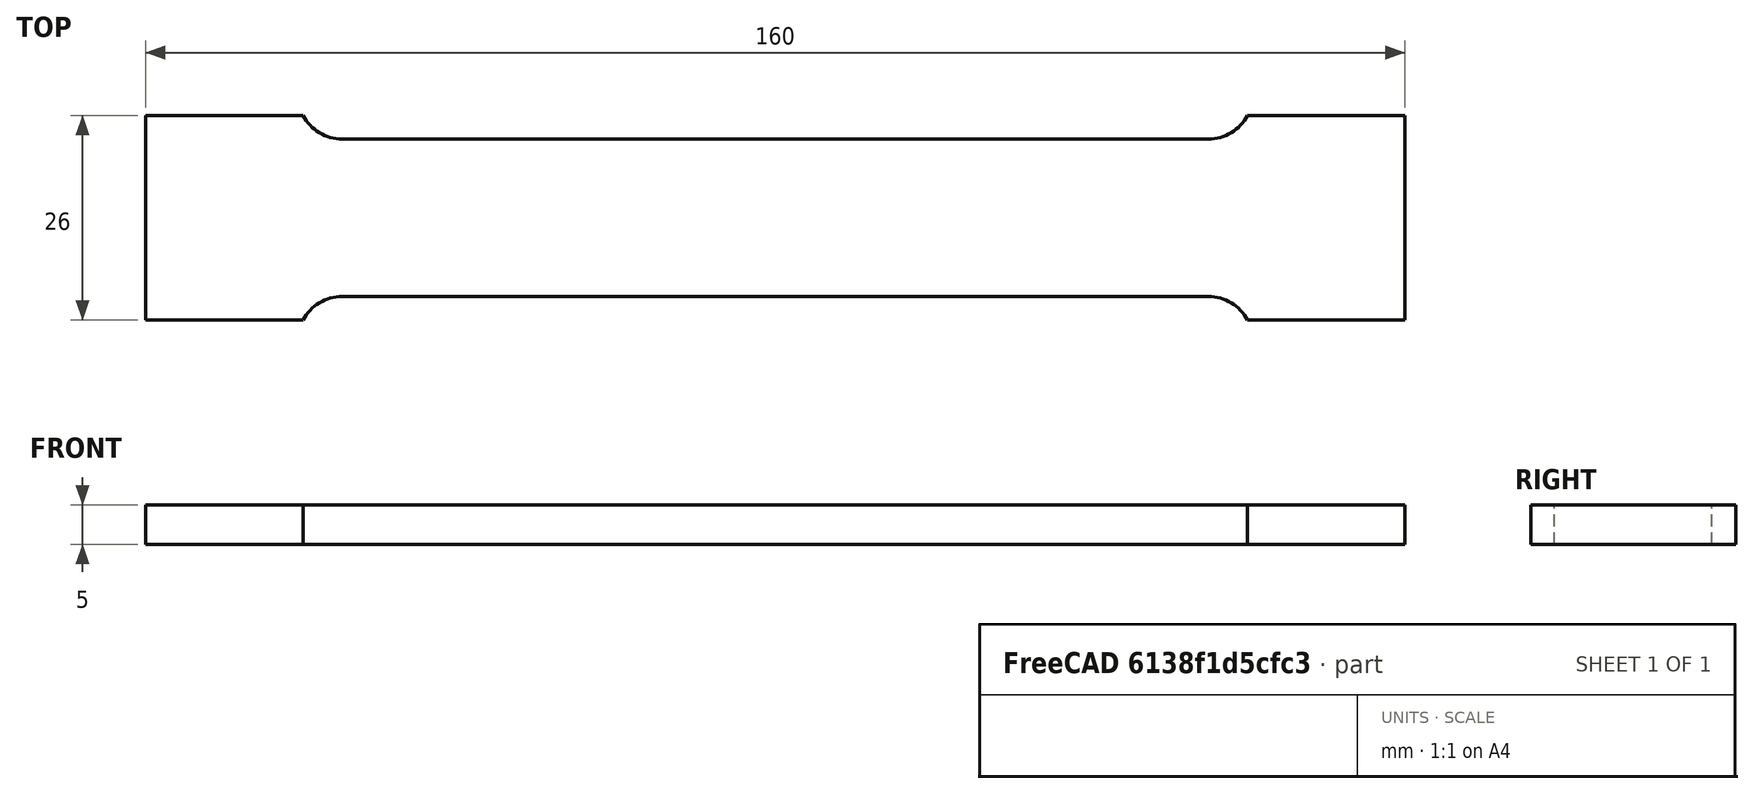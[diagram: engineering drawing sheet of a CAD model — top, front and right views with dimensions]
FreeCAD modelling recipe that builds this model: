
FCSTD DOCUMENT  (FreeCAD 0.17R8046 (Git))
Label: tensile-test-specimen
License: All rights reserved
LicenseURL: http://en.wikipedia.org/wiki/All_rights_reserved
objects: Sketcher::SketchObject×1, PartDesign::Pad×1, PartDesign::Body×1
note: 4 computed .brp shape members not serialized (recipe doc carries the construction recipe); baked Part::Feature solids carry a one-line shape summary decoded from their .brp

FEATURE [Sketcher::SketchObject] Sketch
  MapMode = 5
  Support = -> [XY_Plane]
  sketch-geometry (12):
    g0: LineSegment StartX=-80 StartY=-13 StartZ=0 EndX=-60.002 EndY=-13 EndZ=0
    g1: ArcOfCircle CenterX=-55 CenterY=-15.67 CenterZ=0 NormalX=0 NormalY=0 NormalZ=1 Radius=5.67 StartAngle=1.57079 EndAngle=2.65128
    g2: LineSegment StartX=-80 StartY=13 StartZ=0 EndX=-60 EndY=13 EndZ=0
    g3: ArcOfCircle CenterX=-55 CenterY=15.6667 CenterZ=0 NormalX=0 NormalY=0 NormalZ=1 Radius=5.66667 StartAngle=3.63155 EndAngle=4.71239
    g4: LineSegment StartX=80 StartY=13 StartZ=0 EndX=60.002 EndY=13 EndZ=0
    g5: ArcOfCircle CenterX=55 CenterY=15.67 CenterZ=0 NormalX=0 NormalY=0 NormalZ=1 Radius=5.67 StartAngle=4.71239 EndAngle=5.79288
    g6: LineSegment StartX=80 StartY=-13 StartZ=0 EndX=60.002 EndY=-13 EndZ=0
    g7: ArcOfCircle CenterX=55 CenterY=-15.67 CenterZ=0 NormalX=0 NormalY=0 NormalZ=1 Radius=5.67 StartAngle=0.49031 EndAngle=1.5708
    g8: LineSegment StartX=-80 StartY=13 StartZ=0 EndX=-80 EndY=-13 EndZ=0
    g9: LineSegment StartX=80 StartY=13 StartZ=0 EndX=80 EndY=-13 EndZ=0
    g10: LineSegment StartX=-55 StartY=10 StartZ=0 EndX=55 EndY=10 EndZ=0
    g11: LineSegment StartX=55 StartY=-10 StartZ=0 EndX=-55 EndY=-10 EndZ=0
  constraints (34):
    c: Coincident(g0,g1)
    c: Horizontal(g0)
    c: Coincident(g2,g3)
    c: Horizontal(g2)
    c: Coincident(g4,g5)
    c: Horizontal(g4)
    c: Coincident(g6,g7)
    c: Horizontal(g6)
    c: Radius(g1) = 5.67
    c: DistanceY(g0,g2) = 26
    c: Symmetric(g2,g0,g-1)
    c: DistanceX(g2,g2) = 20
    c: DistanceX(g3,g5) = 110
    c: Symmetric(g7,g5,g-1)
    c: Symmetric(g3,g1,g-1)
    c: Symmetric(g4,g2,g-2)
    c: Symmetric(g6,g0,g-2)
    c: Symmetric(g3,g5,g-2)
    c: Symmetric(g1,g7,g-2)
    c: Symmetric(g7,g5,g-1)
    c: Coincident(g8,g2)
    c: Coincident(g8,g0)
    c: Coincident(g9,g4)
    c: Coincident(g9,g6)
    c: Coincident(g10,g3)
    c: Coincident(g10,g5)
    c: Horizontal(g10)
    c: Tangent(g10,g5)
    c: Coincident(g11,g7)
    c: Coincident(g11,g1)
    c: Horizontal(g11)
    c: DistanceY(g7,g5) = 20
    c: DistanceX(g0,g6) = 160
    c: Tangent(g11,g1)
FEATURE [PartDesign::Pad] Pad
  Length = 5
  Length2 = 100
  Midplane = true
  Profile = -> Sketch
  Type = 0
FEATURE [PartDesign::Body] Body
  Model = -> [Sketch,Pad]
  Origin = -> BodyOrigin
  Tip = -> Pad
